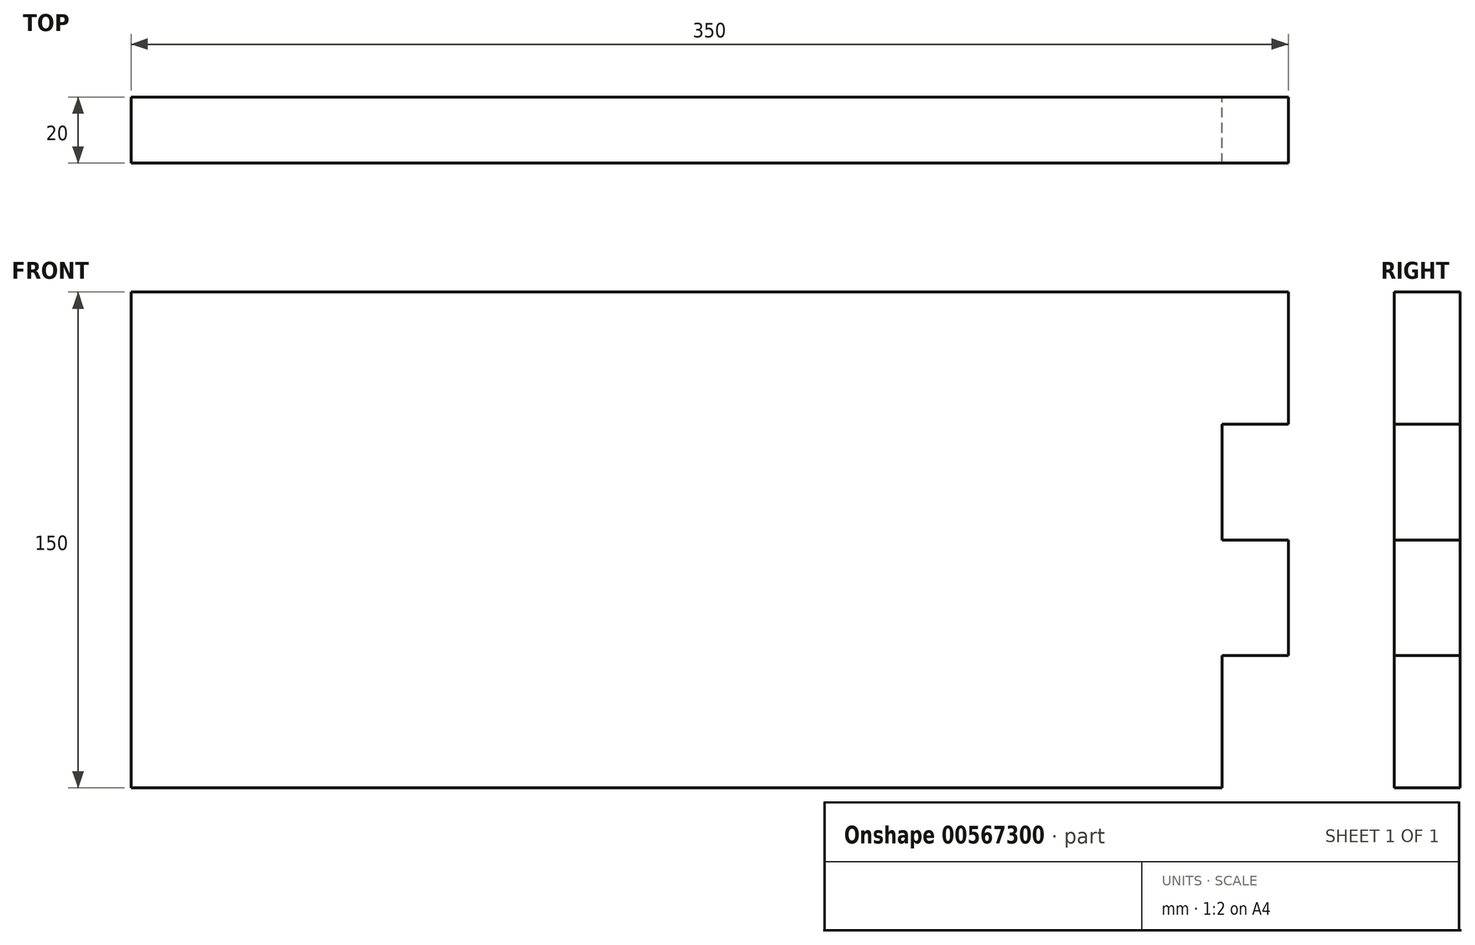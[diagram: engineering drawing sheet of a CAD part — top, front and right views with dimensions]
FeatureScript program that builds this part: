
annotation { "Feature Type Name" : "Feature", "Feature Type Description" : "" }
export const myFeature = defineFeature(function(context is Context, id is Id, definition is map)
    precondition{}
    {
        {
            var Q0;
            Q0=qCreatedBy(makeId("Front.planeOp"),FACE);
            var sketch = newSketch(context, id + "F0", { "sketchPlane" : qUnion([Q0])});
            skLineSegment(sketch, "E0.bottom", {"start": v(-20, 0) * mm, "end": v(-350, 0) * mm});
            skLineSegment(sketch, "E0.top", {"start": v(0, 150) * mm, "end": v(-350, 150) * mm});
            skLineSegment(sketch, "E0.left", {"start": v(0, 40) * mm, "end": v(0, 75) * mm});
            skLineSegment(sketch, "E0.right", {"start": v(-350, 0) * mm, "end": v(-350, 150) * mm});
            skLineSegment(sketch, "E1", {"start": v(-20, 110) * mm, "end": v(-20, 75) * mm});
            skLineSegment(sketch, "E2", {"start": v(0, 75) * mm, "end": v(-20, 75) * mm});
            skLineSegment(sketch, "E3", {"start": v(0, 110) * mm, "end": v(-20, 110) * mm});
            skLineSegment(sketch, "E4", {"start": v(0, 40) * mm, "end": v(-20, 40) * mm});
            skLineSegment(sketch, "E5.trimOffspring", {"start": v(0, 110) * mm, "end": v(0, 150) * mm});
            skPoint(sketch, "E6.orphan", {"position": v(0, 0) * mm});
            skLineSegment(sketch, "E7.trimOffspring", {"start": v(-20, 40) * mm, "end": v(-20, 0) * mm});
            skPoint(sketch, "E8.orphan", {"position": v(-20, 150) * mm});
            skSolve(sketch);
        }
        {
            var Q0;
            Q0 = qSketchRegion(id + "F0", true);
            var Q1;
            Q1=makeQuery(id+"F0.imprint","IMPRINT",FACE,{"disambiguationData":[TD([[makeQuery(id+"F0.imprint","IMPRINT",EDGE,{"derivedFrom":sQuery(id+"F0.wireOp",EDGE,"E0.bottom")}),-1.0]])]});
            extrude(context, id + "F1", {"entities" : qUnion([Q0, Q1]), "depth" : 20 * mm, "offsetDistance" : 25.4 * mm});
        }
    });
